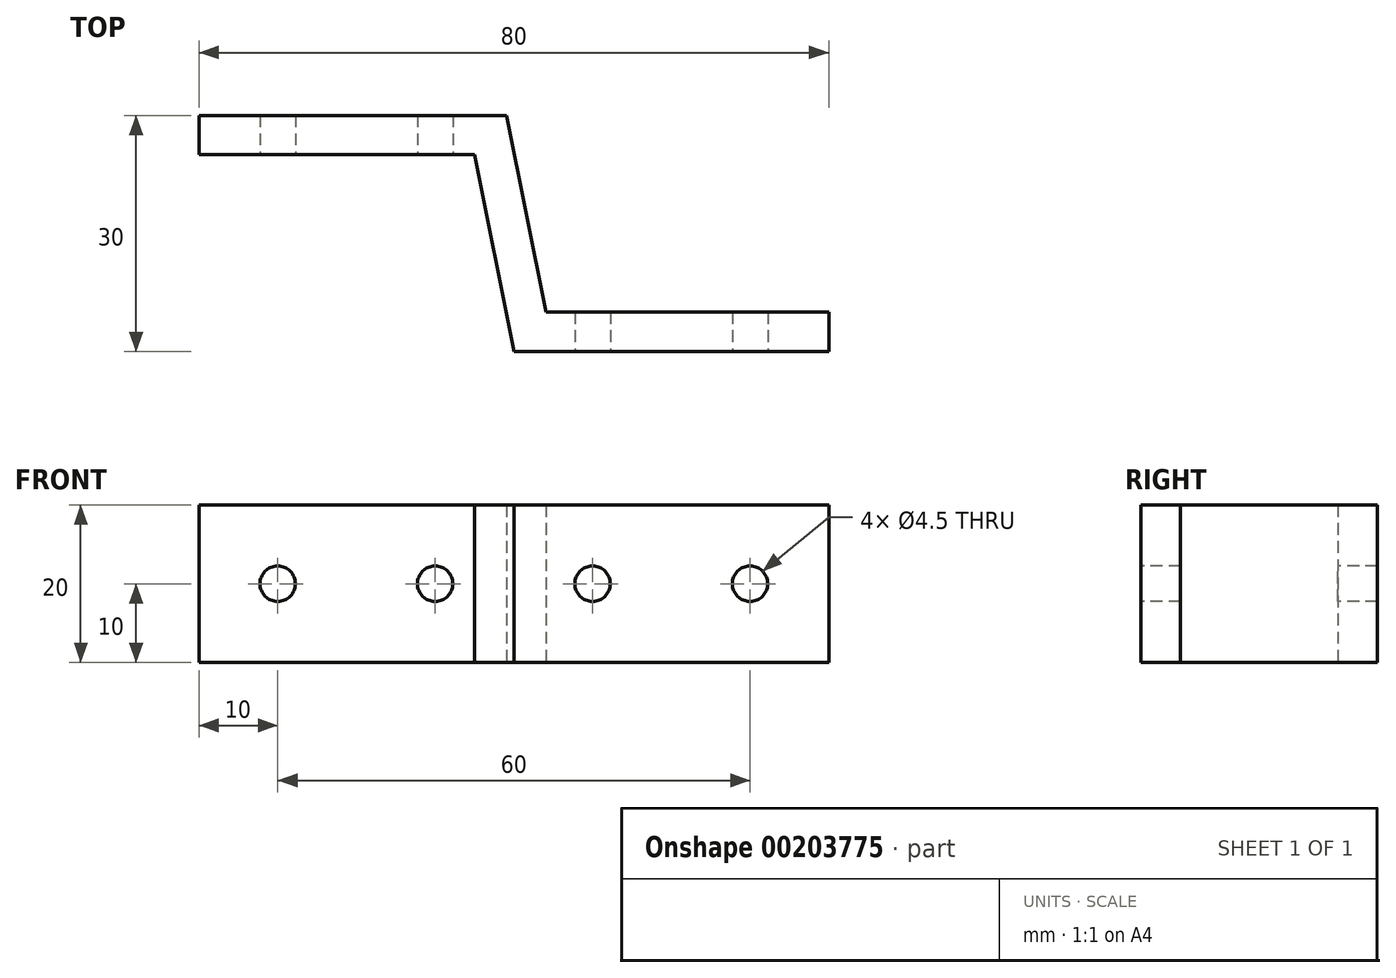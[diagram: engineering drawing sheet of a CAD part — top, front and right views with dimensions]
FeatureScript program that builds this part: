
annotation { "Feature Type Name" : "Feature", "Feature Type Description" : "" }
export const myFeature = defineFeature(function(context is Context, id is Id, definition is map)
    precondition{}
    {
        {
            var Q0;
            Q0=qCreatedBy(makeId("Top.planeOp"),FACE);
            var sketch = newSketch(context, id + "F0", { "sketchPlane" : qUnion([Q0])});
            skLineSegment(sketch, "E0", {"start": v(0, 0) * mm, "end": v(40, 0) * mm, "construction": true});
            skLineSegment(sketch, "E1", {"start": v(40, 0) * mm, "end": v(40, -30) * mm, "construction": true});
            skLineSegment(sketch, "E2", {"start": v(-0.9, 0) * mm, "end": v(-40, 0) * mm});
            skLineSegment(sketch, "E3", {"start": v(-40, 0) * mm, "end": v(-40, -5) * mm});
            skLineSegment(sketch, "E4", {"start": v(-40, -5) * mm, "end": v(-5, -5) * mm});
            skLineSegment(sketch, "E5", {"start": v(40, -30) * mm, "end": v(0, -30) * mm});
            skLineSegment(sketch, "E6", {"start": v(0, -30) * mm, "end": v(-5, -5) * mm});
            skLineSegment(sketch, "E7.0", {"start": v(4.1, -25) * mm, "end": v(-0.9, 0) * mm});
            skLineSegment(sketch, "E8", {"start": v(40, -30) * mm, "end": v(40, -25) * mm});
            skPoint(sketch, "E8.endSnap0", {"position": v(40, -15) * mm});
            skLineSegment(sketch, "E9", {"start": v(40, -25) * mm, "end": v(4.1, -25) * mm});
            skSolve(sketch);
        }
        {
            var Q0;
            Q0=makeQuery(id+"F0.imprint","IMPRINT",FACE,{"disambiguationData":[TD([[makeQuery(id+"F0.imprint","IMPRINT",EDGE,{"derivedFrom":sQuery(id+"F0.wireOp",EDGE,"E2")}),1.0]])]});
            extrude(context, id + "F1", {"entities" : qUnion([Q0]), "depth" : 20 * mm, "offsetDistance" : 25 * mm, "symmetric" : true});
        }
        {
            var Q0;
            Q0=makeQuery(id+"F1.opExtrude","SWEPT_FACE",FACE,{"disambiguationData":[OSD([sQuery(id+"F0.wireOp",EDGE,"E4")])]});
            var sketch = newSketch(context, id + "F2", { "sketchPlane" : qUnion([Q0])});
            skLineSegment(sketch, "E10", {"start": v(-40, 0) * mm, "end": v(-30, 0) * mm, "construction": true});
            skPoint(sketch, "E10.endSnap0", {"position": v(-40, 0) * mm});
            skLineSegment(sketch, "E11", {"start": v(-30, 0) * mm, "end": v(-10, 0) * mm, "construction": true});
            skCircle(sketch, "E12", {"center": v(-30, 0) * mm, "radius": 2.25 * mm});
            skCircle(sketch, "E13", {"center": v(-10, 0) * mm, "radius": 2.25 * mm});
            skSolve(sketch);
        }
        {
            var Q0;
            Q0=makeQuery(id+"F2.imprint","IMPRINT",FACE,{"disambiguationData":[TD([[makeQuery(id+"F2.imprint","IMPRINT",EDGE,{"derivedFrom":sQuery(id+"F2.wireOp",EDGE,"E12")}),1.0]])]});
            var Q1;
            Q1=makeQuery(id+"F2.imprint","IMPRINT",FACE,{"disambiguationData":[TD([[makeQuery(id+"F2.imprint","IMPRINT",EDGE,{"derivedFrom":sQuery(id+"F2.wireOp",EDGE,"E13")}),1.0]])]});
            extrude(context, id + "F3", {"entities" : qUnion([Q0, Q1]), "operationType" : NewBodyOperationType.REMOVE, "endBound" : BoundingType.UP_TO_NEXT, "oppositeDirection" : true, "depth" : 25 * mm, "offsetDistance" : 25 * mm});
        }
        {
            var Q0;
            Q0=makeQuery(id+"F1.opExtrude","SWEPT_FACE",FACE,{"disambiguationData":[OSD([sQuery(id+"F0.wireOp",EDGE,"E5")])]});
            var sketch = newSketch(context, id + "F4", { "sketchPlane" : qUnion([Q0])});
            skLineSegment(sketch, "E14", {"start": v(40, 0) * mm, "end": v(30, 0) * mm, "construction": true});
            skPoint(sketch, "E14.endSnap0", {"position": v(40, 0) * mm});
            skLineSegment(sketch, "E15", {"start": v(30, 0) * mm, "end": v(10, 0) * mm, "construction": true});
            skCircle(sketch, "E16", {"center": v(10, 0) * mm, "radius": 2.25 * mm});
            skCircle(sketch, "E17", {"center": v(30, 0) * mm, "radius": 2.25 * mm});
            skSolve(sketch);
        }
        {
            var Q0;
            Q0=makeQuery(id+"F4.imprint","IMPRINT",FACE,{"disambiguationData":[TD([[makeQuery(id+"F4.imprint","IMPRINT",EDGE,{"derivedFrom":sQuery(id+"F4.wireOp",EDGE,"E16")}),1.0]])]});
            var Q1;
            Q1=makeQuery(id+"F4.imprint","IMPRINT",FACE,{"disambiguationData":[TD([[makeQuery(id+"F4.imprint","IMPRINT",EDGE,{"derivedFrom":sQuery(id+"F4.wireOp",EDGE,"E17")}),1.0]])]});
            extrude(context, id + "F5", {"entities" : qUnion([Q0, Q1]), "operationType" : NewBodyOperationType.REMOVE, "endBound" : BoundingType.UP_TO_NEXT, "oppositeDirection" : true, "depth" : 25 * mm, "offsetDistance" : 25 * mm});
        }
    });
